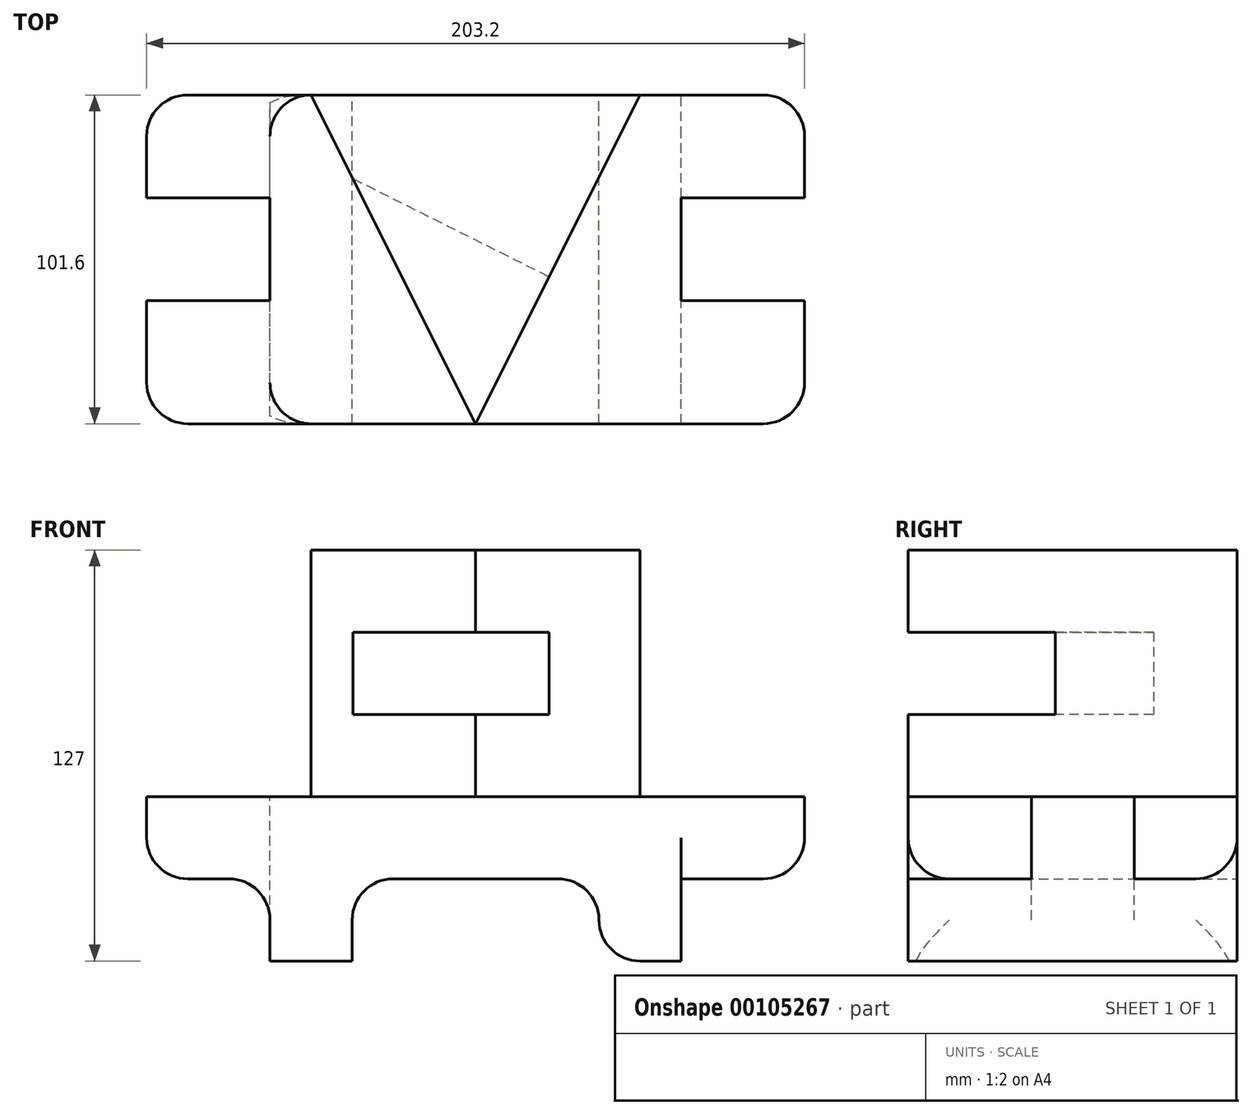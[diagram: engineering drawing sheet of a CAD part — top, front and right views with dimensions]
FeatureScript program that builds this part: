
annotation { "Feature Type Name" : "Feature", "Feature Type Description" : "" }
export const myFeature = defineFeature(function(context is Context, id is Id, definition is map)
    precondition{}
    {
        {
            var Q0;
            Q0=qCreatedBy(makeId("Front.planeOp"),FACE);
            var sketch = newSketch(context, id + "F0", { "sketchPlane" : qUnion([Q0])});
            skLineSegment(sketch, "E0.top", {"start": v(2.55, 25.4) * mm, "end": v(127, 25.4) * mm});
            skLineSegment(sketch, "E1.bottom", {"start": v(-60.95, 50.8) * mm, "end": v(142.25, 50.8) * mm});
            skLineSegment(sketch, "E1.top", {"start": v(-60.95, 25.4) * mm, "end": v(142.25, 25.4) * mm});
            skLineSegment(sketch, "E1.left", {"start": v(-60.95, 50.8) * mm, "end": v(-60.95, 25.4) * mm});
            skLineSegment(sketch, "E1.right", {"start": v(142.25, 50.8) * mm, "end": v(142.25, 25.4) * mm});
            skLineSegment(sketch, "E2", {"start": v(-22.85, 0) * mm, "end": v(-22.85, 25.4) * mm});
            skLineSegment(sketch, "E3", {"start": v(104.15, 25.4) * mm, "end": v(104.15, 0) * mm});
            skLineSegment(sketch, "E4.bottom", {"start": v(-22.85, 0) * mm, "end": v(2.55, 0) * mm});
            skLineSegment(sketch, "E4.top", {"start": v(-22.85, 25.4) * mm, "end": v(2.55, 25.4) * mm});
            skLineSegment(sketch, "E5.bottom", {"start": v(104.15, 0) * mm, "end": v(78.75, 0) * mm});
            skLineSegment(sketch, "E5.top", {"start": v(104.15, 25.4) * mm, "end": v(78.75, 25.4) * mm});
            skLineSegment(sketch, "E5.left", {"start": v(104.15, 0) * mm, "end": v(104.15, 25.4) * mm});
            skLineSegment(sketch, "E6", {"start": v(2.55, 0) * mm, "end": v(2.55, 25.4) * mm});
            skLineSegment(sketch, "E7", {"start": v(78.75, 25.4) * mm, "end": v(78.75, 0) * mm});
            skSolve(sketch);
        }
        {
            var Q0;
            Q0=makeQuery(id+"F0.imprint","IMPRINT",FACE,{"disambiguationData":[TD([[makeQuery(id+"F0.imprint","IMPRINT",EDGE,{"derivedFrom":sQuery(id+"F0.wireOp",EDGE,"E4.bottom")}),1.0]])]});
            var Q1;
            Q1=makeQuery(id+"F0.imprint","IMPRINT",FACE,{"disambiguationData":[TD([[makeQuery(id+"F0.imprint","IMPRINT",EDGE,{"derivedFrom":sQuery(id+"F0.wireOp",EDGE,"E5.bottom")}),-1.0]])]});
            var Q2;
            Q2=makeQuery(id+"F0.imprint","IMPRINT",FACE,{"disambiguationData":[TD([[makeQuery(id+"F0.imprint","IMPRINT",EDGE,{"derivedFrom":sQuery(id+"F0.wireOp",EDGE,"E1.bottom")}),-1.0]])]});
            extrude(context, id + "F1", {"entities" : qUnion([Q0, Q1, Q2]), "endBound" : BoundingType.SYMMETRIC, "depth" : 101.6 * mm});
        }
        {
            var Q0;
            Q0=makeQuery(id+"F1.opExtrude","SWEPT_FACE",FACE,{"disambiguationData":[OSD([sQuery(id+"F0.wireOp",EDGE,"E1.bottom")])]});
            var sketch = newSketch(context, id + "F2", { "sketchPlane" : qUnion([Q0])});
            skLineSegment(sketch, "E8.bottom", {"start": v(-60.95, 19.05) * mm, "end": v(-22.85, 19.05) * mm});
            skLineSegment(sketch, "E8.top", {"start": v(-60.95, -12.7) * mm, "end": v(-22.85, -12.7) * mm});
            skLineSegment(sketch, "E8.left", {"start": v(-60.95, 19.05) * mm, "end": v(-60.95, -12.7) * mm});
            skLineSegment(sketch, "E8.right", {"start": v(-22.85, 19.05) * mm, "end": v(-22.85, -12.7) * mm});
            skLineSegment(sketch, "E9.bottom", {"start": v(142.25, 19.05) * mm, "end": v(104.15, 19.05) * mm});
            skLineSegment(sketch, "E9.top", {"start": v(142.25, -12.7) * mm, "end": v(104.15, -12.7) * mm});
            skLineSegment(sketch, "E9.left", {"start": v(142.25, 19.05) * mm, "end": v(142.25, -12.7) * mm});
            skLineSegment(sketch, "E9.right", {"start": v(104.15, 19.05) * mm, "end": v(104.15, -12.7) * mm});
            skSolve(sketch);
        }
        {
            var Q0;
            Q0=makeQuery(id+"F2.imprint","IMPRINT",FACE,{"disambiguationData":[TD([[makeQuery(id+"F2.imprint","IMPRINT",EDGE,{"derivedFrom":sQuery(id+"F2.wireOp",EDGE,"E8.bottom")}),-1.0]])]});
            var Q1;
            Q1=makeQuery(id+"F2.imprint","IMPRINT",FACE,{"disambiguationData":[TD([[makeQuery(id+"F2.imprint","IMPRINT",EDGE,{"derivedFrom":sQuery(id+"F2.wireOp",EDGE,"E9.bottom")}),1.0]])]});
            extrude(context, id + "F3", {"entities" : qUnion([Q0, Q1]), "operationType" : NewBodyOperationType.REMOVE, "endBound" : BoundingType.THROUGH_ALL, "oppositeDirection" : true, "depth" : 25.4 * mm});
        }
        {
            var Q0;
            Q0=makeQuery(id+"F1.opExtrude","CAP_EDGE",EDGE,{"disambiguationData":[OSD([sQuery(id+"F0.wireOp",EDGE,"E1.right")])],"isStart":false});
            var Q1;
            Q1=makeQuery(id+"F1.opExtrude","CAP_EDGE",EDGE,{"disambiguationData":[OSD([sQuery(id+"F0.wireOp",EDGE,"E1.right")])],"isStart":true});
            var Q2;
            Q2=makeQuery(id+"F1.opExtrude","CAP_EDGE",EDGE,{"disambiguationData":[OSD([sQuery(id+"F0.wireOp",EDGE,"E1.left")])],"isStart":false});
            var Q3;
            Q3=makeQuery(id+"F1.opExtrude","CAP_EDGE",EDGE,{"disambiguationData":[OSD([sQuery(id+"F0.wireOp",EDGE,"E1.left")])],"isStart":true});
            fillet(context, id + "F4", {"entities" : qUnion([Q0, Q1, Q2, Q3]), "radius" : 12.7 * mm, "tangentPropagation" : true, "allowEdgeOverflow" : false});
        }
        {
            var Q0;
            Q0=makeQuery(id+"F1.opExtrude","SWEPT_EDGE",EDGE,{"disambiguationData":[OSD([sQuery(id+"F0.wireOp",EDGE,"E1.top"),sQuery(id+"F0.wireOp",EDGE,"E4.top"),sQuery(id+"F0.wireOp",EDGE,"E6")])]});
            var Q1;
            Q1=makeQuery(id+"F1.opExtrude","SWEPT_EDGE",EDGE,{"disambiguationData":[OSD([sQuery(id+"F0.wireOp",EDGE,"E1.top"),sQuery(id+"F0.wireOp",EDGE,"E5.top"),sQuery(id+"F0.wireOp",EDGE,"E7")])]});
            fillet(context, id + "F5", {"entities" : qUnion([Q0, Q1]), "radius" : 12.7 * mm, "tangentPropagation" : true, "allowEdgeOverflow" : false});
        }
        {
            var Q0;
            Q0=makeQuery(id+"F1.opExtrude","SWEPT_FACE",FACE,{"disambiguationData":[OSD([sQuery(id+"F0.wireOp",EDGE,"E1.bottom")])]});
            var sketch = newSketch(context, id + "F6", { "sketchPlane" : qUnion([Q0])});
            skLineSegment(sketch, "E10", {"start": v(40.65, 50.8) * mm, "end": v(91.45, 50.8) * mm});
            skLineSegment(sketch, "E11", {"start": v(91.45, 50.8) * mm, "end": v(40.65, 50.8) * mm});
            skLineSegment(sketch, "E12", {"start": v(40.65, 50.8) * mm, "end": v(-10.15, 50.8) * mm});
            skLineSegment(sketch, "E13", {"start": v(-10.15, 50.8) * mm, "end": v(40.65, -50.8) * mm});
            skLineSegment(sketch, "E14", {"start": v(40.65, -50.8) * mm, "end": v(91.45, 50.8) * mm});
            skSolve(sketch);
        }
        {
            var Q0;
            Q0 = qSketchRegion(id + "F6", true);
            extrude(context, id + "F7", {"entities" : qUnion([Q0]), "operationType" : NewBodyOperationType.ADD, "depth" : 76.2 * mm});
        }
        {
            var Q0;
            Q0=makeQuery(id+"F7.opExtrude","SWEPT_FACE",FACE,{"disambiguationData":[OSD([sQuery(id+"F6.wireOp",EDGE,"E14")])]});
            var sketch = newSketch(context, id + "F8", { "sketchPlane" : qUnion([Q0])});
            skLineSegment(sketch, "E15", {"start": v(-27.26, 101.6) * mm, "end": v(23.54, 101.6) * mm});
            skLineSegment(sketch, "E16", {"start": v(23.54, 101.6) * mm, "end": v(23.54, 76.2) * mm});
            skLineSegment(sketch, "E17", {"start": v(23.54, 76.2) * mm, "end": v(-27.26, 76.2) * mm});
            skSolve(sketch);
        }
        {
            var Q0;
            Q0 = qSketchRegion(id + "F8", true);
            var Q1;
            {var subQ0=sQuery(id+"F8.wireOp",EDGE,"E15");Q1=makeQuery(id+"F8.imprint","IMPRINT",FACE,{"disambiguationData":[TD([[makeQuery(id+"F8.imprint","IMPRINT",EDGE,{"derivedFrom":subQ0}),-1.0]])]});}
            extrude(context, id + "F9", {"entities" : qUnion([Q0, Q1]), "operationType" : NewBodyOperationType.REMOVE, "endBound" : BoundingType.THROUGH_ALL, "oppositeDirection" : true, "depth" : 25.4 * mm});
        }
    });
